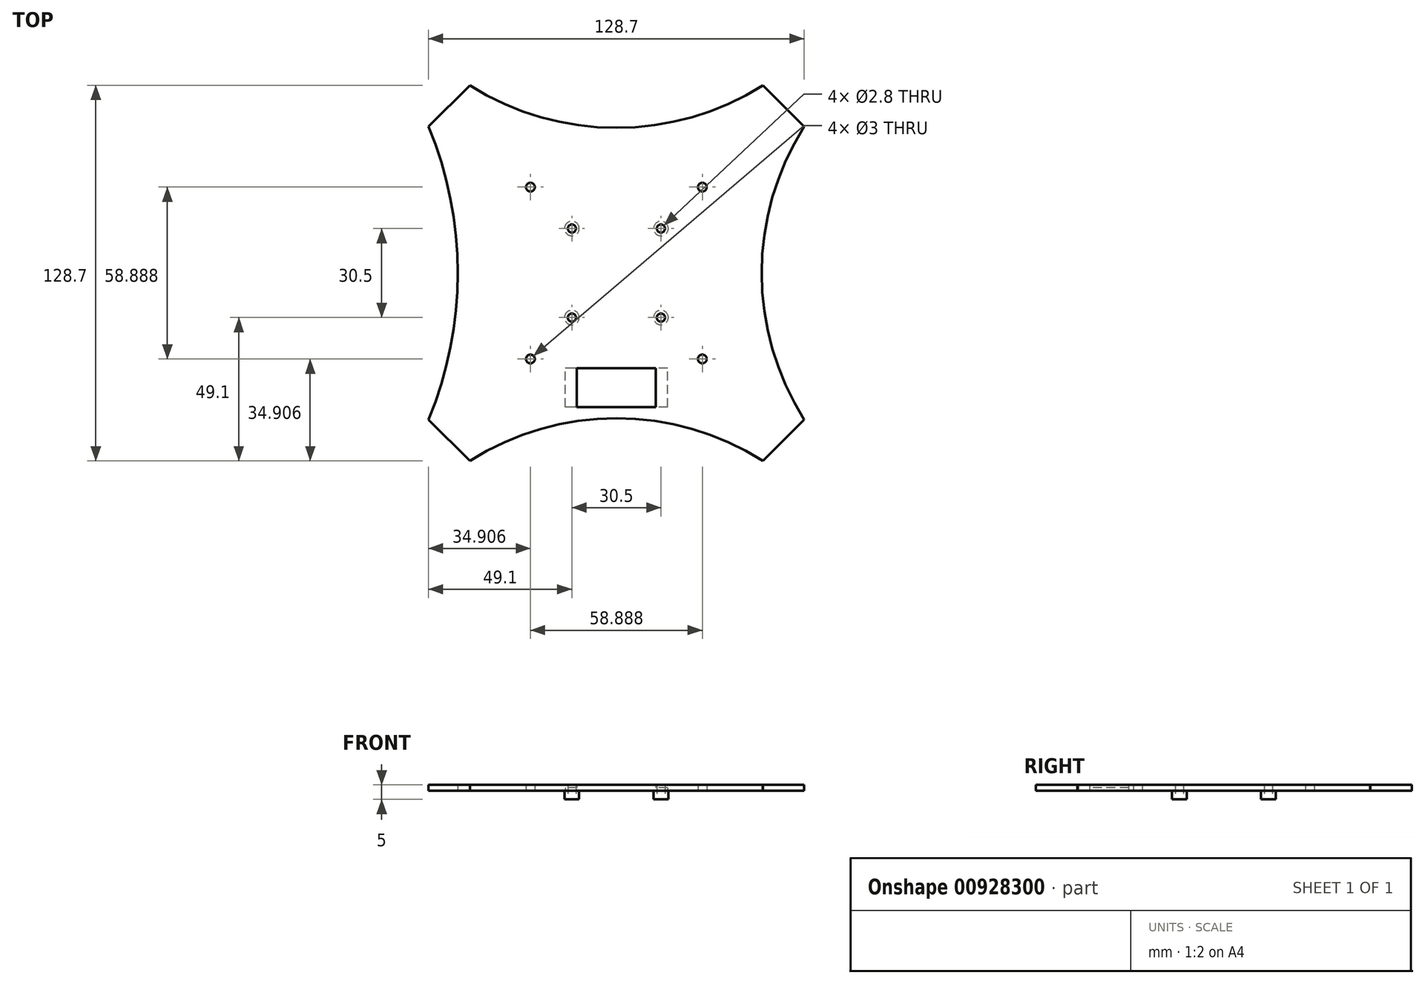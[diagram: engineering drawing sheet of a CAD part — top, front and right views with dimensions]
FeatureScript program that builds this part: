
annotation { "Feature Type Name" : "Feature", "Feature Type Description" : "" }
export const myFeature = defineFeature(function(context is Context, id is Id, definition is map)
    precondition{}
    {
        {
            var Q0;
            Q0=qCreatedBy(makeId("Top.planeOp"),FACE);
            var sketch = newSketch(context, id + "F0", { "sketchPlane" : qUnion([Q0])});
            skLineSegment(sketch, "E0", {"start": v(-50.2, 64.35) * mm, "end": v(-64.35, 50.2) * mm});
            skLineSegment(sketch, "E1", {"start": v(-64.35, -50.2) * mm, "end": v(-50.2, -64.35) * mm});
            skLineSegment(sketch, "E2", {"start": v(50.2, 64.35) * mm, "end": v(64.35, 50.2) * mm});
            skLineSegment(sketch, "E3", {"start": v(64.35, -50.2) * mm, "end": v(50.2, -64.35) * mm});
            skArc(sketch, "E4", {"start": v(-64.35, -50.2) * mm, "mid": v(-54.37, 0) * mm, "end": v(-64.35, 50.2) * mm});
            skArc(sketch, "E5", {"start": v(-50.2, 64.35) * mm, "mid": v(0, 49.76) * mm, "end": v(50.2, 64.35) * mm});
            skArc(sketch, "E6", {"start": v(64.35, 50.2) * mm, "mid": v(49.76, 0) * mm, "end": v(64.35, -50.2) * mm});
            skArc(sketch, "E7", {"start": v(50.2, -64.35) * mm, "mid": v(0, -49.76) * mm, "end": v(-50.2, -64.35) * mm});
            skPoint(sketch, "E8.middle", {"position": v(0, 0) * mm});
            skCircle(sketch, "E9", {"center": v(-15.25, 15.25) * mm, "radius": 2.5 * mm});
            skCircle(sketch, "E10", {"center": v(15.25, 15.25) * mm, "radius": 2.5 * mm});
            skCircle(sketch, "E11", {"center": v(15.25, -15.25) * mm, "radius": 2.5 * mm});
            skCircle(sketch, "E12", {"center": v(-15.25, -15.25) * mm, "radius": 2.5 * mm});
            skCircle(sketch, "E13", {"center": v(-15.25, 15.25) * mm, "radius": 1.4 * mm});
            skCircle(sketch, "E14", {"center": v(15.25, 15.25) * mm, "radius": 1.4 * mm});
            skCircle(sketch, "E15", {"center": v(-15.25, -15.25) * mm, "radius": 1.4 * mm});
            skCircle(sketch, "E16", {"center": v(15.25, -15.25) * mm, "radius": 1.4 * mm});
            skLineSegment(sketch, "E17.bottom", {"start": v(17.55, -45.93) * mm, "end": v(-17.55, -45.93) * mm});
            skLineSegment(sketch, "E17.top", {"start": v(17.55, -32.63) * mm, "end": v(-17.55, -32.63) * mm});
            skLineSegment(sketch, "E17.left", {"start": v(17.55, -45.93) * mm, "end": v(17.55, -32.63) * mm});
            skLineSegment(sketch, "E17.right", {"start": v(-17.55, -45.93) * mm, "end": v(-17.55, -32.63) * mm});
            skPoint(sketch, "E17.middle", {"position": v(0, -39.28) * mm});
            skLineSegment(sketch, "E18", {"start": v(-13.55, -32.63) * mm, "end": v(-13.55, -45.93) * mm});
            skLineSegment(sketch, "E19", {"start": v(13.55, -32.63) * mm, "end": v(13.55, -45.93) * mm});
            skLineSegment(sketch, "E20", {"start": v(0, 0) * mm, "end": v(-63.75, 63.75) * mm});
            skLineSegment(sketch, "E21", {"start": v(0, 0) * mm, "end": v(61.31, 61.31) * mm});
            skLineSegment(sketch, "E22", {"start": v(0, 0) * mm, "end": v(62.25, -62.25) * mm});
            skLineSegment(sketch, "E23", {"start": v(0, 0) * mm, "end": v(-63.77, -63.77) * mm});
            skPoint(sketch, "E24", {"position": v(29.44, 29.44) * mm});
            skPoint(sketch, "E25", {"position": v(-29.44, 29.44) * mm});
            skPoint(sketch, "E26", {"position": v(-29.44, -29.44) * mm});
            skPoint(sketch, "E27", {"position": v(29.44, -29.44) * mm});
            skCircle(sketch, "E28", {"center": v(-29.44, 29.44) * mm, "radius": 1.5 * mm});
            skCircle(sketch, "E29", {"center": v(29.44, 29.44) * mm, "radius": 1.5 * mm});
            skCircle(sketch, "E30", {"center": v(-29.44, -29.44) * mm, "radius": 1.5 * mm});
            skCircle(sketch, "E31", {"center": v(29.44, -29.44) * mm, "radius": 1.5 * mm});
            skSolve(sketch);
        }
        {
            var Q0;
            {var subQ0=sQuery(id+"F0.wireOp",EDGE,"E17.left");Q0=makeQuery(id+"F0.imprint","IMPRINT",FACE,{"disambiguationData":[TD([[makeQuery(id+"F0.imprint","IMPRINT",EDGE,{"derivedFrom":subQ0}),1.0]])]});}
            var Q1;
            {var subQ0=sQuery(id+"F0.wireOp",EDGE,"E17.right");Q1=makeQuery(id+"F0.imprint","IMPRINT",FACE,{"disambiguationData":[TD([[makeQuery(id+"F0.imprint","IMPRINT",EDGE,{"derivedFrom":subQ0}),-1.0]])]});}
            var Q2;
            Q2=makeQuery(id+"F0.imprint","IMPRINT",FACE,{"disambiguationData":[TD([[makeQuery(id+"F0.imprint","IMPRINT",EDGE,{"derivedFrom":sQuery(id+"F0.wireOp",EDGE,"E0")}),1.0]])]});
            var Q3;
            Q3=makeQuery(id+"F0.imprint","IMPRINT",FACE,{"disambiguationData":[TD([[makeQuery(id+"F0.imprint","IMPRINT",EDGE,{"derivedFrom":sQuery(id+"F0.wireOp",EDGE,"E9")}),1.0]])]});
            var Q4;
            Q4=makeQuery(id+"F0.imprint","IMPRINT",FACE,{"disambiguationData":[TD([[makeQuery(id+"F0.imprint","IMPRINT",EDGE,{"derivedFrom":sQuery(id+"F0.wireOp",EDGE,"E10")}),1.0]])]});
            var Q5;
            Q5=makeQuery(id+"F0.imprint","IMPRINT",FACE,{"disambiguationData":[TD([[makeQuery(id+"F0.imprint","IMPRINT",EDGE,{"derivedFrom":sQuery(id+"F0.wireOp",EDGE,"E11")}),1.0]])]});
            var Q6;
            Q6=makeQuery(id+"F0.imprint","IMPRINT",FACE,{"disambiguationData":[TD([[makeQuery(id+"F0.imprint","IMPRINT",EDGE,{"derivedFrom":sQuery(id+"F0.wireOp",EDGE,"E12")}),1.0]])]});
            var Q7;
            {var subQ5=sQuery(id+"F0.wireOp",EDGE,"E6");Q7=makeQuery(id+"F0.imprint","IMPRINT",FACE,{"disambiguationData":[TD([[makeQuery(id+"F0.imprint","IMPRINT",EDGE,{"derivedFrom":subQ5}),-1.0]])]});}
            var Q8;
            {var subQ10=sQuery(id+"F0.wireOp",EDGE,"E7");Q8=makeQuery(id+"F0.imprint","IMPRINT",FACE,{"disambiguationData":[TD([[makeQuery(id+"F0.imprint","IMPRINT",EDGE,{"derivedFrom":subQ10}),-1.0]])]});}
            extrude(context, id + "F1", {"entities" : qUnion([Q0, Q1, Q2, Q3, Q4, Q5, Q6, Q7, Q8]), "depth" : 2 * mm, "offsetDistance" : 25 * mm});
        }
        {
            var Q0;
            Q0=makeQuery(id+"F0.imprint","IMPRINT",FACE,{"disambiguationData":[TD([[makeQuery(id+"F0.imprint","IMPRINT",EDGE,{"derivedFrom":sQuery(id+"F0.wireOp",EDGE,"E9")}),1.0]])]});
            var Q1;
            Q1=makeQuery(id+"F0.imprint","IMPRINT",FACE,{"disambiguationData":[TD([[makeQuery(id+"F0.imprint","IMPRINT",EDGE,{"derivedFrom":sQuery(id+"F0.wireOp",EDGE,"E10")}),1.0]])]});
            var Q2;
            Q2=makeQuery(id+"F0.imprint","IMPRINT",FACE,{"disambiguationData":[TD([[makeQuery(id+"F0.imprint","IMPRINT",EDGE,{"derivedFrom":sQuery(id+"F0.wireOp",EDGE,"E12")}),1.0]])]});
            var Q3;
            Q3=makeQuery(id+"F0.imprint","IMPRINT",FACE,{"disambiguationData":[TD([[makeQuery(id+"F0.imprint","IMPRINT",EDGE,{"derivedFrom":sQuery(id+"F0.wireOp",EDGE,"E11")}),1.0]])]});
            extrude(context, id + "F2", {"entities" : qUnion([Q0, Q1, Q2, Q3]), "operationType" : NewBodyOperationType.ADD, "oppositeDirection" : true, "depth" : 3 * mm, "offsetDistance" : 25 * mm});
        }
        {
            var Q0;
            Q0=makeQuery(id+"F0.imprint","IMPRINT",FACE,{"disambiguationData":[TD([[makeQuery(id+"F0.imprint","IMPRINT",EDGE,{"derivedFrom":sQuery(id+"F0.wireOp",EDGE,"E17.bottom")}),-1.0]])]});
            extrude(context, id + "F3", {"entities" : qUnion([Q0]), "operationType" : NewBodyOperationType.REMOVE, "depth" : 1 * mm, "offsetDistance" : 25 * mm});
        }
    });
